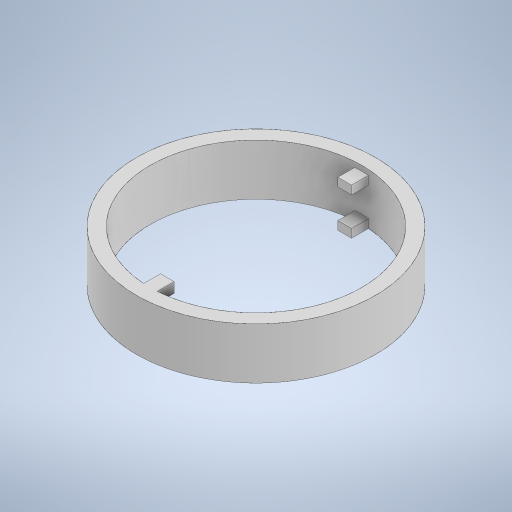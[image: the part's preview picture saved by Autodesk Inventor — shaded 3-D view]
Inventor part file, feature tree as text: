
AUTODESK INVENTOR PART (.ipt)
format: ipt  version: 2023 (Build 270158000, 158)  size: 291,328 bytes
history: native  units: in
note: dims shown in document units (in); Inventor stores cm internally (conversion verified against a paired STEP export)
features: extrude x4, sketch x4
ambient origin geometry x8: Origin, YZ Plane, XZ Plane, XY Plane, X Axis, Y Axis, Z Axis, Center Point
bodies: Solid1 (feature_tree)
feature tree (8):
  extrude  "Extrusion1"  Depth=2.7559in
  extrude  "Extrusion3"  Depth=0.5906in
  extrude  "Extrusion4"  Depth=0.0787in
  extrude  "Extrusion5"  Depth=0.5906in
  sketch  "Sketch1"  dims[d0=2.4409in d1=2.7559in]
  sketch  "Sketch3"  dims[d2=0.5906in d3=0.0in d4=0.1969in]
  sketch  "Sketch4"  dims[d5=0.0787in d6=0.0787in]
  sketch  "Sketch5"  dims[d7=0.1969in d8=0.0787in d9=0.0787in d14=0.1969in d15=0.0787in d16=0.0787in d17=0.5315in d18=0.0in d19=0.1673in d20=0.1673in d21=0.5315in d22=0.0in d23=0.1772in d24=0.1772in d25=0.5906in d26=0.0in]
